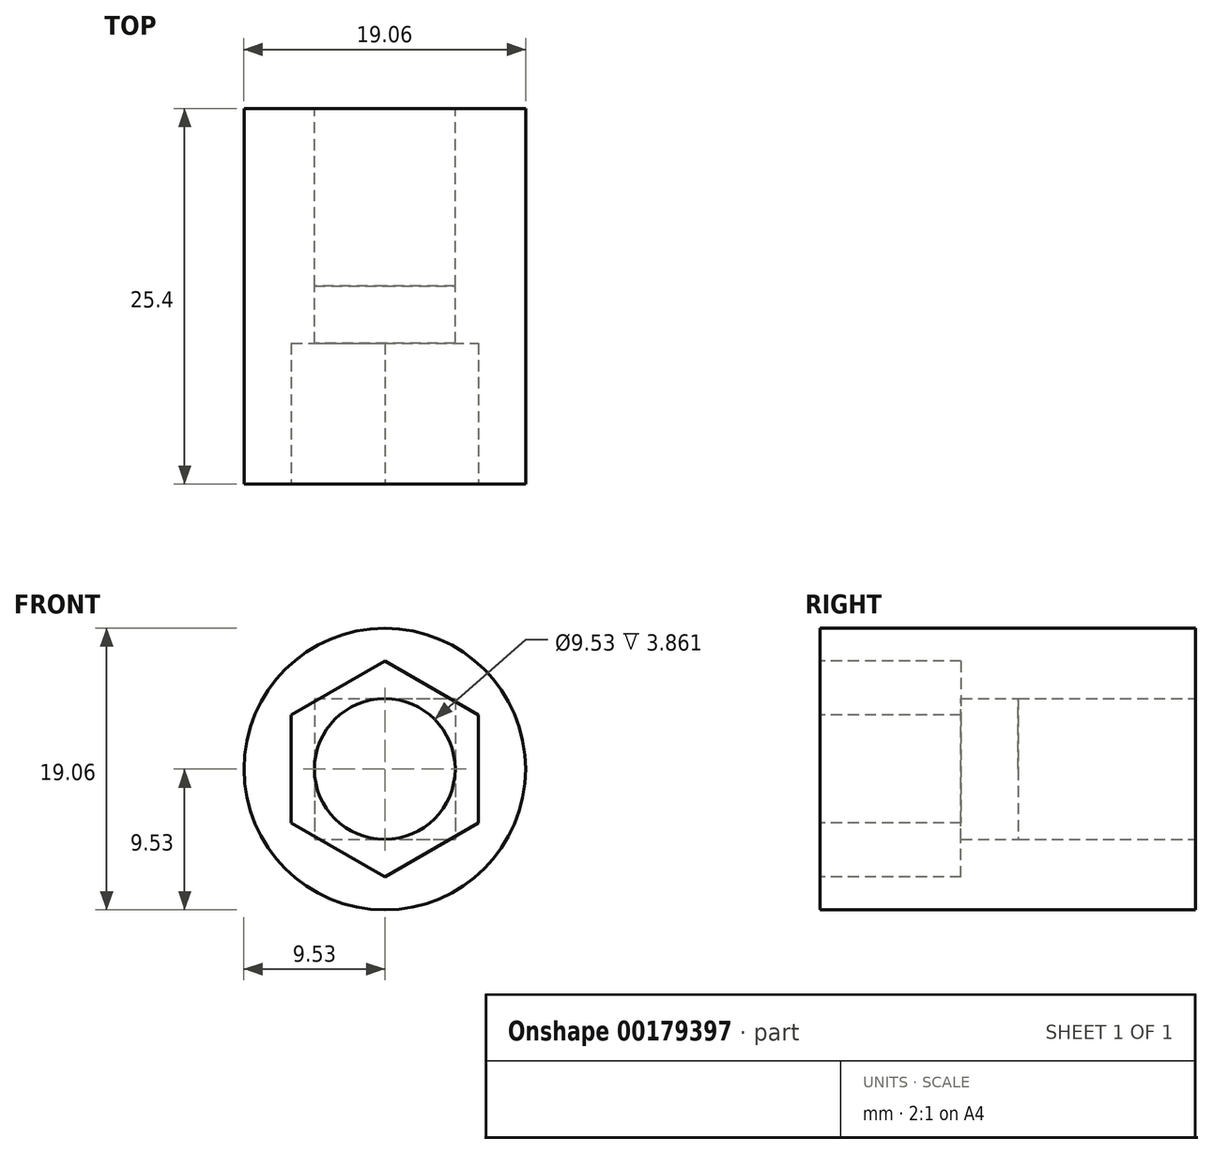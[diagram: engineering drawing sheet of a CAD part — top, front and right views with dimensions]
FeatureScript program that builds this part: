
annotation { "Feature Type Name" : "Feature", "Feature Type Description" : "" }
export const myFeature = defineFeature(function(context is Context, id is Id, definition is map)
    precondition{}
    {
        {
            var Q0;
            Q0=qCreatedBy(makeId("Front.planeOp"),FACE);
            var sketch = newSketch(context, id + "F0", { "sketchPlane" : qUnion([Q0])});
            skCircle(sketch, "E0", {"center": v(0, 0) * mm, "radius": 9.53 * mm});
            skSolve(sketch);
        }
        {
            var Q0;
            Q0 = qSketchRegion(id + "F0", true);
            extrude(context, id + "F1", {"entities" : qUnion([Q0]), "depth" : 25.4 * mm});
        }
        {
            var Q0;
            Q0=qCreatedBy(makeId("Front.planeOp"),FACE);
            var sketch = newSketch(context, id + "F2", { "sketchPlane" : qUnion([Q0])});
            skLineSegment(sketch, "E1.bottom", {"start": v(-4.76, 4.76) * mm, "end": v(4.76, 4.76) * mm});
            skLineSegment(sketch, "E1.top", {"start": v(-4.76, -4.76) * mm, "end": v(4.76, -4.76) * mm});
            skLineSegment(sketch, "E1.left", {"start": v(-4.76, 4.76) * mm, "end": v(-4.76, -4.76) * mm});
            skLineSegment(sketch, "E1.right", {"start": v(4.76, 4.76) * mm, "end": v(4.76, -4.76) * mm});
            skPoint(sketch, "E1.middle", {"position": v(0, 0) * mm});
            skCircle(sketch, "E2", {"center": v(0, 0) * mm, "radius": 4.76 * mm});
            skSolve(sketch);
        }
        {
            var Q0;
            {var subQ0=sQuery(id+"F2.wireOp",EDGE,"E2");var subQ1=makeQuery(id+"F2.imprint","INTERSECT",VERTEX,{"derivedFrom":[sQuery(id+"F2.wireOp",EDGE,"E1.bottom"),subQ0]});Q0=makeQuery(id+"F2.imprint","IMPRINT",FACE,{"disambiguationData":[TD([[makeQuery(id+"F2.imprint","IMPRINT",EDGE,{"disambiguationData":[TD([[subQ1,1.0]])],"derivedFrom":subQ0}),1.0]])]});}
            extrude(context, id + "F3", {"entities" : qUnion([Q0]), "operationType" : NewBodyOperationType.REMOVE, "endBound" : BoundingType.THROUGH_ALL, "depth" : 25.4 * mm});
        }
        {
            var Q0;
            Q0 = qSketchRegion(id + "F2", true);
            extrude(context, id + "F4", {"entities" : qUnion([Q0]), "operationType" : NewBodyOperationType.REMOVE, "depth" : 12 * mm});
        }
        {
            var Q0;
            Q0=makeQuery(id+"F1.opExtrude","CAP_FACE",FACE,{"disambiguationData":[OSD([sQuery(id+"F0.wireOp",EDGE,"E0")])],"isStart":false});
            var sketch = newSketch(context, id + "F5", { "sketchPlane" : qUnion([Q0])});
            skCircle(sketch, "E3.cCircle", {"center": v(0, 0) * mm, "radius": 6.32 * mm, "construction": true});
            skLineSegment(sketch, "E3.0", {"start": v(6.32, 3.65) * mm, "end": v(6.32, -3.65) * mm});
            skLineSegment(sketch, "E3.1", {"start": v(6.32, -3.65) * mm, "end": v(0, -7.3) * mm});
            skLineSegment(sketch, "E3.2", {"start": v(0, -7.3) * mm, "end": v(-6.32, -3.65) * mm});
            skLineSegment(sketch, "E3.3", {"start": v(-6.32, -3.65) * mm, "end": v(-6.32, 3.65) * mm});
            skLineSegment(sketch, "E3.4", {"start": v(-6.32, 3.65) * mm, "end": v(0, 7.3) * mm});
            skLineSegment(sketch, "E3.5", {"start": v(0, 7.3) * mm, "end": v(6.32, 3.65) * mm});
            skPoint(sketch, "E3.0.midPoint", {"position": v(6.32, 0) * mm});
            skSolve(sketch);
        }
        {
            var Q0;
            Q0 = qSketchRegion(id + "F5", true);
            extrude(context, id + "F6", {"entities" : qUnion([Q0]), "operationType" : NewBodyOperationType.REMOVE, "flatOperationType" : FlatOperationType.REMOVE, "oppositeDirection" : true, "offsetDistance" : 25.4 * mm, "depth" : 9.52 * mm, "domain" : OperationDomain.MODEL});
        }
    });
